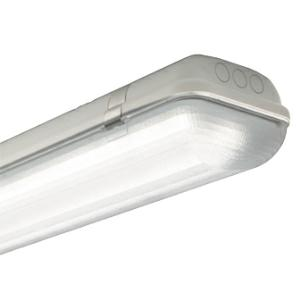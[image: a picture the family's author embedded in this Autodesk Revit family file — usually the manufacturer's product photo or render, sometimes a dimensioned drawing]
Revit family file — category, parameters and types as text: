
# Revit family: 3f_filippi_-_3f_linda_3f_filippi_-_58602_-_3f_linda_led_2x24w-830_ep_l1270
name_source: partatom
category: Lighting Fixtures
units: mm (PartAtom-declared; Revit-internal decimal feet)

## family parameters
Cut with Voids When Loaded = No
Host = Face
Light Source = No
Part Type = Normal
Room Calculation Point = No
Round Connector Dimension = Use Diameter
Shared = No

## types (1)
- 3F Filippi - 3F Linda (1 x LED, 7515 lm, 55.5 W, 3000 K)
    Apparent Load = 56 VA
    Approval mark = ENEC
    CIE Flux Codes = 46 76 93 97 100
    Color Rendering = 80
    Color Temperature = 3000 K
    Control Gear = Electronic ballast
    Default Elevation = 1800 mm
    Description = ILLUMINOTECHNICAL
Luminous efficiency 100% (DLOR 97%, ULOR 3%).
Initial luminous flux of the luminaire 7515 lm.
Emergency luminaire luminous flux BLF 7.1%.
Controlled symmetric distribution.
Installation Interdistance Transv.D = 1.52 x hu - Long.D = 1.17 x hu.
Tabular UGR (CIE 117 - 4H-8H; S=0.25H; 70/50/20): RUG 24.2 - 23.3.
Beam angle: 94° - 78°.
Luminous efficacy 135 lm/W.
Lifetime (L93/B10): 30000 h. (tq+25°C)
Lifetime (L90/B10): 50000 h. (tq+25°C)
Lifetime (L85/B10): 80000 h. (tq+25°C)
Lifetime (L80/B10): 100000 h. (tq+25°C)
Sudden decreased luminous flux after 50000 hours: 0% (C0).
Photobiological safety in compliance with IEC/TR 62778: RG0 risk exempt, (IEC 62471).
In compliance with IEC/EN 62722-2-1 - IEC/EN 62717 standards.

SOURCE
2 linear LED modules 24W/830.
Energy efficiency class (UE 2019/2020 - UE 2019/2015): D.
CIE 13.3 Colour rendering index: CRI >80 (R9 <50%).
IES TM-30 Fidelity Index: Rf = 84 Rg = 95.
CCT nominal colour temperature 3000 K.
Colour initial tolerance (MacAdam): SDCM 3.

MECHANICAL
Self-extinguishing V2 polycarbonate housing, injection moulded, RAL 7035 grey.
Ecologic anti-aging injected sealing gasket.
Diffuser in self-extinguishing V2 polycarbonate, photo-engraved interior, UV stabilised, injection moulded with smooth outer surface, tamper-proof opening.
Gear-holder reflector in hot-dip galvanised steel, painted with white polyester base.
Snug fit safety snap-lock clips for diffuser mounting in stainless steel, screwdriver opening.
Fixing brackets in stainless steel.
Possibility for technicians to access the interior of the luminaire.
Luminaire with limited surface temperature. - D - (EN 60598-2-24)
Dimensions: 1270x160 mm, height 100 mm. Weight 3.06 kg.
IP66 protection degree.
Mechanical strength to impacts IK10 (20 joule).
Glow-wire test resistance 850°C.

ELECTRICAL
Halogen Free electronic wiring 230V-50/60Hz, power factor 0.90, THD <25%, constant output current, SELV, class I, 1 driver.
Power of the luminaire 55.5 W.
CE - IEC 60598-1 - EN 60598-1.
EP maintained emergency wiring on board, 1h duration, 24h recharge; compliant with EN 60598-2-22, excluding high risk areas.
SAFE FLICKER: PstLM=<1 and SVM=<0.4 (IEC TR 61547-1 and IEC TR 63158), to ensure a more comfortable and safe light.
Ambient temperature from +5°C to +25°C.
Temperature class T6 max 85°C.
Relative humidity UR: <85%.

INSTALLATION
Ceiling / Suspended / Wall.
All accessories dedicated to this product are available on the Catalog and on our website www.3F-Filippi.com.

APPLICATIONS
Suitable product for food production plants (HACCP), IFS (Food Version 6), BRC (GSFS Food Version 7).
Dry, dusty indoor environments, subject to occasional water splashes.
Virtually shatterproof polycarbonate compatibly with the fumes / atmospheres that compromise the elasticity of plastic materials.
Not suitable for installation on surfaces subject to important vibrations, exposed to weather conditions, on ropes or poles.
Suitable for illumination of public car parks and parking grounds referred to DIN 67528:2018-04.

WARNING
Fixture not suitable for cold stores with an ambient temperature <5°C and/or relative humidity >85%.
Luminaire designed for disposal/recycling at end-of-life.
Replaceable (LED only) light source by a professional. Replaceable control gear by a professional.
    Height = 100 mm  [stored 0.328084 ft]
    Lamp = 1 x LED
    Lamp Light Flux = 7515 lm
    Lamp Power = 55.5 W
    Lamp count = 1
    Length = 1270 mm
    Lifetime = 50000 h
    Luminous efficacy = 135 lm/W
    Manufacturer = 3F Filippi
    ModVariant = No
    Model = 3F Filippi - 58602 - 3F Linda LED 2x24W-830 EP L1270
    Mounting Place = Ceiling
    Mounting Type = Pendant
    Number of Poles = 1
    OnlyDefault = Yes
    Power Factor = 1
    Product Name = 3F Filippi - 3F Linda
    Product group = pendant luminaire
    ProductGroupID = 9
    Protection Class = Protection class I
    Protection Degree = IP 66
    RLX_Detail_Level = 1
    RLX_Emergency_Light_Flux = 0 lm
    RLX_Emergency_Type = 0
    RLX_Emergency_Type_DB = No
    RlxData = <blob elided: 72077 chars, md5=6eaf13fb>
    Socket = socket
    Standby Power = 0 W
    System Light Flux = 7515 lm
    System Power = 56 W
    Type Comments = Product without accessories
    Type Image = 3ffilippi_58602.jpg
    URL = http://relux.com
    VarID = ---
    Voltage = 0 V
    Weight = 0.00 kg
    Width = 160 mm

note: [stored X ft] marks values corroborated as IEEE doubles in the binary element streams (Revit-internal decimal feet)

## geometry (parser evidence)
native form markers: Blend x4, Sweep x9
no freeform markers — native parametric forms only
